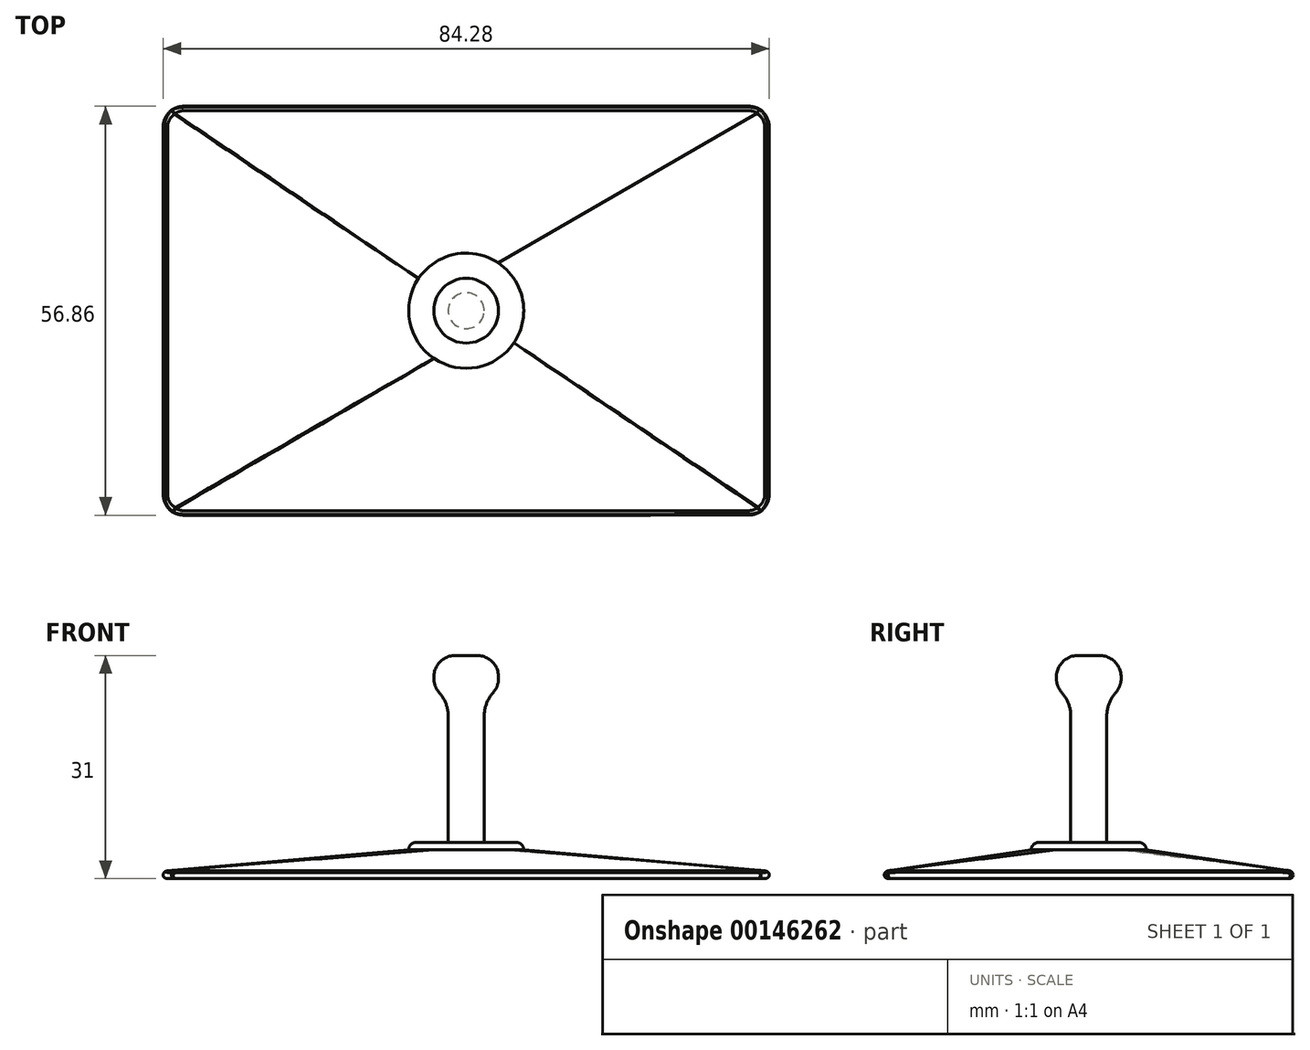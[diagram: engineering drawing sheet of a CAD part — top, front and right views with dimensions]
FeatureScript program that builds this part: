
annotation { "Feature Type Name" : "Feature", "Feature Type Description" : "" }
export const myFeature = defineFeature(function(context is Context, id is Id, definition is map)
    precondition{}
    {
        {
            var Q0;
            Q0=qCreatedBy(makeId("Top.planeOp"),FACE);
            var sketch = newSketch(context, id + "F0", { "sketchPlane" : qUnion([Q0])});
            skLineSegment(sketch, "E0.bottom", {"start": v(42.25, -28.5) * mm, "end": v(-42.25, -28.5) * mm});
            skLineSegment(sketch, "E0.top", {"start": v(42.25, 28.5) * mm, "end": v(-42.25, 28.5) * mm});
            skLineSegment(sketch, "E0.left", {"start": v(42.25, -28.5) * mm, "end": v(42.25, 28.5) * mm});
            skLineSegment(sketch, "E0.right", {"start": v(-42.25, -28.5) * mm, "end": v(-42.25, 28.5) * mm});
            skPoint(sketch, "E0.middle", {"position": v(0, 0) * mm});
            skSolve(sketch);
        }
        {
            var Q0;
            Q0=makeQuery(id+"F0.imprint","IMPRINT",FACE,{"disambiguationData":[TD([[makeQuery(id+"F0.imprint","IMPRINT",EDGE,{"derivedFrom":sQuery(id+"F0.wireOp",EDGE,"E0.bottom")}),-1.0]])]});
            var Q1;
            Q1 = qBodyType(qCreatedBy(id + "F2" ,EDGE), BodyType.WIRE);
            cPlane(context, id + "F1", {"entities" : qUnion([Q0, Q1]), "cplaneType" : CPlaneType.OFFSET, "offset" : 5 * mm, "width" : 150 * mm, "height" : 150 * mm});
        }
        {
            var Q0;
            Q0=qCreatedBy(id+"F1.planeOp",FACE);
            var sketch = newSketch(context, id + "F2", { "sketchPlane" : qUnion([Q0])});
            skCircle(sketch, "E1", {"center": v(0, 0) * mm, "radius": 8 * mm});
            skSolve(sketch);
        }
        {
            var Q0;
            Q0=makeQuery(id+"F2.imprint","IMPRINT",FACE,{"disambiguationData":[TD([[makeQuery(id+"F2.imprint","IMPRINT",EDGE,{"derivedFrom":sQuery(id+"F2.wireOp",EDGE,"E1")}),1.0]])]});
            extrude(context, id + "F3", {"entities" : qUnion([Q0]), "oppositeDirection" : true, "depth" : 1 * mm});
        }
        {
            var Q0;
            Q0=makeQuery(id+"F0.imprint","IMPRINT",FACE,{"disambiguationData":[TD([[makeQuery(id+"F0.imprint","IMPRINT",EDGE,{"derivedFrom":sQuery(id+"F0.wireOp",EDGE,"E0.bottom")}),-1.0]])]});
            extrude(context, id + "F4", {"entities" : qUnion([Q0]), "depth" : 1 * mm});
        }
        {
            var Q1;
            Q1=makeQuery(id+"F4.opExtrude","CAP_FACE",FACE,{"disambiguationData":[OSD([sQuery(id+"F0.wireOp",EDGE,"E0.bottom"),sQuery(id+"F0.wireOp",EDGE,"E0.top"),sQuery(id+"F0.wireOp",EDGE,"E0.left"),sQuery(id+"F0.wireOp",EDGE,"E0.right")])],"isStart":false});
            var Q2;
            Q2=makeQuery(id+"F3.opExtrude","CAP_FACE",FACE,{"disambiguationData":[OSD([sQuery(id+"F2.wireOp",EDGE,"E1")])],"isStart":false});
            loft(context, id + "F5", {"operationType" : NewBodyOperationType.ADD, "sheetProfilesArray" : [{ "sheetProfileEntities" : qUnion([Q1]) }, { "sheetProfileEntities" : qUnion([Q2]) }]});
        }
        {
            var Q0;
            Q0=makeQuery(id+"F3.opExtrude","CAP_FACE",FACE,{"disambiguationData":[OSD([sQuery(id+"F2.wireOp",EDGE,"E1")])],"isStart":true});
            var sketch = newSketch(context, id + "F6", { "sketchPlane" : qUnion([Q0])});
            skCircle(sketch, "E2", {"center": v(0, 0) * mm, "radius": 2.5 * mm});
            skSolve(sketch);
        }
        {
            var Q0;
            Q0 = qSketchRegion(id + "F6", true);
            extrude(context, id + "F7", {"entities" : qUnion([Q0]), "operationType" : NewBodyOperationType.ADD, "depth" : 20 * mm});
        }
        {
            var Q0;
            Q0=makeQuery(id+"F7.opExtrude","CAP_FACE",FACE,{"disambiguationData":[OSD([sQuery(id+"F6.wireOp",EDGE,"E2")])],"isStart":false});
            var sketch = newSketch(context, id + "F8", { "sketchPlane" : qUnion([Q0])});
            skCircle(sketch, "E3", {"center": v(0, 0) * mm, "radius": 4.5 * mm});
            skSolve(sketch);
        }
        {
            var Q0;
            Q0 = qSketchRegion(id + "F8", true);
            extrude(context, id + "F9", {"entities" : qUnion([Q0]), "operationType" : NewBodyOperationType.ADD, "depth" : 6 * mm});
        }
        {
            var Q0;
            Q0=makeQuery(id+"F9.opExtrude","CAP_EDGE",EDGE,{"disambiguationData":[OSD([sQuery(id+"F8.wireOp",EDGE,"E3")])],"isStart":false});
            var Q1;
            Q1=makeQuery(id+"F9.opExtrude","CAP_EDGE",EDGE,{"disambiguationData":[OSD([sQuery(id+"F8.wireOp",EDGE,"E3")])],"isStart":true});
            fillet(context, id + "F10", {"entities" : qUnion([Q0, Q1]), "radius" : 3 * mm, "tangentPropagation" : true, "allowEdgeOverflow" : false});
        }
        {
            var Q0;
            Q0=makeQuery(id+"F10.opFillet","BLEND_EDGE",EDGE,{"blendedFrom":[makeQuery(id+"F9.opExtrude","CAP_EDGE",EDGE,{"disambiguationData":[OSD([sQuery(id+"F8.wireOp",EDGE,"E3")])],"isStart":true}),makeQuery(id+"F7.opExtrude","SWEPT_FACE",FACE,{"disambiguationData":[OSD([sQuery(id+"F6.wireOp",EDGE,"E2")])]})],"blendedInto":[makeQuery(id+"F7.opExtrude","SWEPT_FACE",FACE,{"disambiguationData":[OSD([sQuery(id+"F6.wireOp",EDGE,"E2")])]})]});
            var Q1;
            Q1=makeQuery(id+"F7.opExtrude","CAP_EDGE",EDGE,{"disambiguationData":[OSD([sQuery(id+"F6.wireOp",EDGE,"E2")])],"isStart":true});
            fillet(context, id + "F11", {"entities" : qUnion([Q0, Q1]), "radius" : 5 * mm, "tangentPropagation" : true, "allowEdgeOverflow" : false});
        }
        {
            var Q0;
            Q0=makeQuery(id+"F3.opExtrude","CAP_EDGE",EDGE,{"disambiguationData":[OSD([sQuery(id+"F2.wireOp",EDGE,"E1")])],"isStart":true});
            fillet(context, id + "F12", {"entities" : qUnion([Q0]), "radius" : 1 * mm, "tangentPropagation" : true, "allowEdgeOverflow" : false});
        }
        {
            var Q0;
            Q0=makeQuery(id+"F5.opLoft","SWEPT_EDGE",EDGE,{"disambiguationData":[OSD([sQuery(id+"F0.wireOp",EDGE,"E0.bottom"),sQuery(id+"F0.wireOp",EDGE,"E0.left")])]});
            var Q1;
            Q1=makeQuery(id+"F5.opLoft","SWEPT_EDGE",EDGE,{"disambiguationData":[OSD([sQuery(id+"F0.wireOp",EDGE,"E0.bottom"),sQuery(id+"F0.wireOp",EDGE,"E0.top"),sQuery(id+"F0.wireOp",EDGE,"E0.right"),sQuery(id+"F2.wireOp",EDGE,"E1")])]});
            var Q2;
            Q2=makeQuery(id+"F5.opLoft","SWEPT_EDGE",EDGE,{"disambiguationData":[OSD([sQuery(id+"F0.wireOp",EDGE,"E0.bottom"),sQuery(id+"F0.wireOp",EDGE,"E0.top"),sQuery(id+"F0.wireOp",EDGE,"E0.left"),sQuery(id+"F2.wireOp",EDGE,"E1")])]});
            var Q3;
            Q3=makeQuery(id+"F5.opLoft","SWEPT_EDGE",EDGE,{"disambiguationData":[OSD([sQuery(id+"F0.wireOp",EDGE,"E0.top"),sQuery(id+"F0.wireOp",EDGE,"E0.left"),sQuery(id+"F0.wireOp",EDGE,"E0.right"),sQuery(id+"F2.wireOp",EDGE,"E1")])]});
            fillet(context, id + "F13", {"entities" : qUnion([Q0, Q1, Q2, Q3]), "radius" : 1 * mm, "tangentPropagation" : true, "allowEdgeOverflow" : false});
        }
        {
            var Q0;
            Q0=makeQuery(id+"F4.opExtrude","SWEPT_EDGE",EDGE,{"disambiguationData":[OSD([sQuery(id+"F0.wireOp",EDGE,"E0.bottom"),sQuery(id+"F0.wireOp",EDGE,"E0.right")])]});
            var Q1;
            Q1=makeQuery(id+"F4.opExtrude","SWEPT_EDGE",EDGE,{"disambiguationData":[OSD([sQuery(id+"F0.wireOp",EDGE,"E0.top"),sQuery(id+"F0.wireOp",EDGE,"E0.right")])]});
            var Q2;
            Q2=makeQuery(id+"F4.opExtrude","SWEPT_EDGE",EDGE,{"disambiguationData":[OSD([sQuery(id+"F0.wireOp",EDGE,"E0.bottom"),sQuery(id+"F0.wireOp",EDGE,"E0.left")])]});
            var Q3;
            Q3=makeQuery(id+"F4.opExtrude","SWEPT_EDGE",EDGE,{"disambiguationData":[OSD([sQuery(id+"F0.wireOp",EDGE,"E0.top"),sQuery(id+"F0.wireOp",EDGE,"E0.left")])]});
            fillet(context, id + "F14", {"entities" : qUnion([Q0, Q1, Q2, Q3]), "radius" : 3 * mm, "tangentPropagation" : true, "allowEdgeOverflow" : false});
        }
        {
            var Q0;
            {var subQ0=sQuery(id+"F0.wireOp",EDGE,"E0.right");Q0=makeQuery(id+"F5.boolean.opBoolean","MERGE",EDGE,{"derivedFrom":[makeQuery(id+"F4.opExtrude","CAP_EDGE",EDGE,{"disambiguationData":[OSD([subQ0])],"isStart":false}),makeQuery(id+"F5.opLoft","MID_CAP_EDGE",EDGE,{"disambiguationData":[OSD([sQuery(id+"F0.wireOp",EDGE,"E0.bottom"),sQuery(id+"F0.wireOp",EDGE,"E0.top"),subQ0])],"capPos":0.0})]});}
            var Q1;
            {var subQ0=sQuery(id+"F0.wireOp",EDGE,"E0.right");var subQ1=sQuery(id+"F0.wireOp",EDGE,"E0.top");var subQ2=sQuery(id+"F0.wireOp",EDGE,"E0.left");var subQ3=sQuery(id+"F0.wireOp",EDGE,"E0.bottom");var subQ4=sQuery(id+"F2.wireOp",EDGE,"E1");Q1=makeQuery(id+"F14.opFillet","BLEND_EDGE",EDGE,{"blendedFrom":[makeQuery(id+"F4.opExtrude","SWEPT_EDGE",EDGE,{"disambiguationData":[OSD([subQ3,subQ0])]}),makeQuery(id+"F5.opLoft","SWEPT_FACE",FACE,{"disambiguationData":[OSD([subQ3,subQ1,subQ2,subQ0,subQ4]),TDD([makeQuery(id+"F3.opExtrude","CAP_EDGE",EDGE,{"disambiguationData":[OSD([subQ4])],"isStart":false}),makeQuery(id+"F4.opExtrude","CAP_VERTEX",VERTEX,{"disambiguationData":[OSD([subQ3,subQ0])],"isStart":false}),makeQuery(id+"F4.opExtrude","CAP_VERTEX",VERTEX,{"disambiguationData":[OSD([subQ1,subQ2])],"isStart":false}),makeQuery(id+"F4.opExtrude","CAP_VERTEX",VERTEX,{"disambiguationData":[OSD([subQ1,subQ0])],"isStart":false}),makeQuery(id+"F4.opExtrude","CAP_EDGE",EDGE,{"disambiguationData":[OSD([subQ0])],"isStart":false})])]})],"blendedInto":[makeQuery(id+"F5.opLoft","SWEPT_FACE",FACE,{"disambiguationData":[OSD([subQ3,subQ1,subQ2,subQ0,subQ4]),TDD([makeQuery(id+"F3.opExtrude","CAP_EDGE",EDGE,{"disambiguationData":[OSD([subQ4])],"isStart":false}),makeQuery(id+"F4.opExtrude","CAP_VERTEX",VERTEX,{"disambiguationData":[OSD([subQ3,subQ0])],"isStart":false}),makeQuery(id+"F4.opExtrude","CAP_VERTEX",VERTEX,{"disambiguationData":[OSD([subQ1,subQ2])],"isStart":false}),makeQuery(id+"F4.opExtrude","CAP_VERTEX",VERTEX,{"disambiguationData":[OSD([subQ1,subQ0])],"isStart":false}),makeQuery(id+"F4.opExtrude","CAP_EDGE",EDGE,{"disambiguationData":[OSD([subQ0])],"isStart":false})])]})]});}
            var Q2;
            {var subQ0=sQuery(id+"F0.wireOp",EDGE,"E0.bottom");var subQ1=sQuery(id+"F0.wireOp",EDGE,"E0.right");var subQ2=sQuery(id+"F0.wireOp",EDGE,"E0.top");var subQ3=sQuery(id+"F0.wireOp",EDGE,"E0.left");var subQ4=sQuery(id+"F2.wireOp",EDGE,"E1");Q2=makeQuery(id+"F14.opFillet","BLEND_EDGE",EDGE,{"blendedFrom":[makeQuery(id+"F4.opExtrude","SWEPT_EDGE",EDGE,{"disambiguationData":[OSD([subQ0,subQ1])]}),makeQuery(id+"F5.opLoft","SWEPT_FACE",FACE,{"disambiguationData":[OSD([subQ0,subQ2,subQ3,subQ1,subQ4]),TDD([makeQuery(id+"F3.opExtrude","CAP_EDGE",EDGE,{"disambiguationData":[OSD([subQ4])],"isStart":false}),makeQuery(id+"F4.opExtrude","CAP_VERTEX",VERTEX,{"disambiguationData":[OSD([subQ0,subQ3])],"isStart":false}),makeQuery(id+"F4.opExtrude","CAP_VERTEX",VERTEX,{"disambiguationData":[OSD([subQ0,subQ1])],"isStart":false}),makeQuery(id+"F4.opExtrude","CAP_VERTEX",VERTEX,{"disambiguationData":[OSD([subQ2,subQ1])],"isStart":false}),makeQuery(id+"F4.opExtrude","CAP_EDGE",EDGE,{"disambiguationData":[OSD([subQ0])],"isStart":false})])]})],"blendedInto":[makeQuery(id+"F5.opLoft","SWEPT_FACE",FACE,{"disambiguationData":[OSD([subQ0,subQ2,subQ3,subQ1,subQ4]),TDD([makeQuery(id+"F3.opExtrude","CAP_EDGE",EDGE,{"disambiguationData":[OSD([subQ4])],"isStart":false}),makeQuery(id+"F4.opExtrude","CAP_VERTEX",VERTEX,{"disambiguationData":[OSD([subQ0,subQ3])],"isStart":false}),makeQuery(id+"F4.opExtrude","CAP_VERTEX",VERTEX,{"disambiguationData":[OSD([subQ0,subQ1])],"isStart":false}),makeQuery(id+"F4.opExtrude","CAP_VERTEX",VERTEX,{"disambiguationData":[OSD([subQ2,subQ1])],"isStart":false}),makeQuery(id+"F4.opExtrude","CAP_EDGE",EDGE,{"disambiguationData":[OSD([subQ0])],"isStart":false})])]})]});}
            var Q3;
            {var subQ0=sQuery(id+"F0.wireOp",EDGE,"E0.bottom");Q3=makeQuery(id+"F5.boolean.opBoolean","MERGE",EDGE,{"derivedFrom":[makeQuery(id+"F4.opExtrude","CAP_EDGE",EDGE,{"disambiguationData":[OSD([subQ0])],"isStart":false}),makeQuery(id+"F5.opLoft","MID_CAP_EDGE",EDGE,{"disambiguationData":[OSD([subQ0,sQuery(id+"F0.wireOp",EDGE,"E0.left"),sQuery(id+"F0.wireOp",EDGE,"E0.right")])],"capPos":0.0})]});}
            var Q4;
            {var subQ0=sQuery(id+"F0.wireOp",EDGE,"E0.bottom");var subQ1=sQuery(id+"F0.wireOp",EDGE,"E0.right");var subQ2=sQuery(id+"F0.wireOp",EDGE,"E0.top");var subQ3=sQuery(id+"F0.wireOp",EDGE,"E0.left");var subQ4=sQuery(id+"F2.wireOp",EDGE,"E1");Q4=makeQuery(id+"F14.opFillet","BLEND_EDGE",EDGE,{"blendedFrom":[makeQuery(id+"F4.opExtrude","SWEPT_EDGE",EDGE,{"disambiguationData":[OSD([subQ0,subQ3])]}),makeQuery(id+"F5.opLoft","SWEPT_FACE",FACE,{"disambiguationData":[OSD([subQ0,subQ2,subQ3,subQ1,subQ4]),TDD([makeQuery(id+"F3.opExtrude","CAP_EDGE",EDGE,{"disambiguationData":[OSD([subQ4])],"isStart":false}),makeQuery(id+"F4.opExtrude","CAP_VERTEX",VERTEX,{"disambiguationData":[OSD([subQ0,subQ3])],"isStart":false}),makeQuery(id+"F4.opExtrude","CAP_VERTEX",VERTEX,{"disambiguationData":[OSD([subQ0,subQ1])],"isStart":false}),makeQuery(id+"F4.opExtrude","CAP_VERTEX",VERTEX,{"disambiguationData":[OSD([subQ2,subQ1])],"isStart":false}),makeQuery(id+"F4.opExtrude","CAP_EDGE",EDGE,{"disambiguationData":[OSD([subQ0])],"isStart":false})])]})],"blendedInto":[makeQuery(id+"F5.opLoft","SWEPT_FACE",FACE,{"disambiguationData":[OSD([subQ0,subQ2,subQ3,subQ1,subQ4]),TDD([makeQuery(id+"F3.opExtrude","CAP_EDGE",EDGE,{"disambiguationData":[OSD([subQ4])],"isStart":false}),makeQuery(id+"F4.opExtrude","CAP_VERTEX",VERTEX,{"disambiguationData":[OSD([subQ0,subQ3])],"isStart":false}),makeQuery(id+"F4.opExtrude","CAP_VERTEX",VERTEX,{"disambiguationData":[OSD([subQ0,subQ1])],"isStart":false}),makeQuery(id+"F4.opExtrude","CAP_VERTEX",VERTEX,{"disambiguationData":[OSD([subQ2,subQ1])],"isStart":false}),makeQuery(id+"F4.opExtrude","CAP_EDGE",EDGE,{"disambiguationData":[OSD([subQ0])],"isStart":false})])]})]});}
            var Q5;
            {var subQ0=sQuery(id+"F0.wireOp",EDGE,"E0.left");var subQ1=sQuery(id+"F0.wireOp",EDGE,"E0.bottom");Q5=makeQuery(id+"F14.opFillet","BLEND_EDGE",EDGE,{"blendedFrom":[makeQuery(id+"F4.opExtrude","SWEPT_EDGE",EDGE,{"disambiguationData":[OSD([subQ1,subQ0])]}),makeQuery(id+"F5.opLoft","SWEPT_FACE",FACE,{"disambiguationData":[OSD([subQ1,sQuery(id+"F0.wireOp",EDGE,"E0.top"),subQ0,sQuery(id+"F2.wireOp",EDGE,"E1")])]})],"blendedInto":[makeQuery(id+"F5.opLoft","SWEPT_FACE",FACE,{"disambiguationData":[OSD([subQ1,sQuery(id+"F0.wireOp",EDGE,"E0.top"),subQ0,sQuery(id+"F2.wireOp",EDGE,"E1")])]})]});}
            var Q6;
            {var subQ0=sQuery(id+"F0.wireOp",EDGE,"E0.left");Q6=makeQuery(id+"F5.boolean.opBoolean","MERGE",EDGE,{"derivedFrom":[makeQuery(id+"F4.opExtrude","CAP_EDGE",EDGE,{"disambiguationData":[OSD([subQ0])],"isStart":false}),makeQuery(id+"F5.opLoft","MID_CAP_EDGE",EDGE,{"disambiguationData":[OSD([sQuery(id+"F0.wireOp",EDGE,"E0.bottom"),sQuery(id+"F0.wireOp",EDGE,"E0.top"),subQ0])],"capPos":0.0})]});}
            var Q7;
            {var subQ0=sQuery(id+"F0.wireOp",EDGE,"E0.left");var subQ1=sQuery(id+"F0.wireOp",EDGE,"E0.top");Q7=makeQuery(id+"F14.opFillet","BLEND_EDGE",EDGE,{"blendedFrom":[makeQuery(id+"F4.opExtrude","SWEPT_EDGE",EDGE,{"disambiguationData":[OSD([subQ1,subQ0])]}),makeQuery(id+"F5.opLoft","SWEPT_FACE",FACE,{"disambiguationData":[OSD([sQuery(id+"F0.wireOp",EDGE,"E0.bottom"),subQ1,subQ0,sQuery(id+"F2.wireOp",EDGE,"E1")])]})],"blendedInto":[makeQuery(id+"F5.opLoft","SWEPT_FACE",FACE,{"disambiguationData":[OSD([sQuery(id+"F0.wireOp",EDGE,"E0.bottom"),subQ1,subQ0,sQuery(id+"F2.wireOp",EDGE,"E1")])]})]});}
            var Q8;
            {var subQ0=sQuery(id+"F0.wireOp",EDGE,"E0.top");Q8=makeQuery(id+"F5.boolean.opBoolean","MERGE",EDGE,{"derivedFrom":[makeQuery(id+"F4.opExtrude","CAP_EDGE",EDGE,{"disambiguationData":[OSD([subQ0])],"isStart":false}),makeQuery(id+"F5.opLoft","MID_CAP_EDGE",EDGE,{"disambiguationData":[OSD([subQ0,sQuery(id+"F0.wireOp",EDGE,"E0.left"),sQuery(id+"F0.wireOp",EDGE,"E0.right")])],"capPos":0.0})]});}
            var Q9;
            {var subQ0=sQuery(id+"F0.wireOp",EDGE,"E0.top");var subQ1=sQuery(id+"F0.wireOp",EDGE,"E0.right");var subQ2=sQuery(id+"F0.wireOp",EDGE,"E0.left");var subQ3=sQuery(id+"F0.wireOp",EDGE,"E0.bottom");var subQ4=sQuery(id+"F2.wireOp",EDGE,"E1");Q9=makeQuery(id+"F14.opFillet","BLEND_EDGE",EDGE,{"blendedFrom":[makeQuery(id+"F4.opExtrude","SWEPT_EDGE",EDGE,{"disambiguationData":[OSD([subQ0,subQ2])]}),makeQuery(id+"F5.opLoft","SWEPT_FACE",FACE,{"disambiguationData":[OSD([subQ3,subQ0,subQ2,subQ1,subQ4]),TDD([makeQuery(id+"F3.opExtrude","CAP_EDGE",EDGE,{"disambiguationData":[OSD([subQ4])],"isStart":false}),makeQuery(id+"F4.opExtrude","CAP_VERTEX",VERTEX,{"disambiguationData":[OSD([subQ3,subQ2])],"isStart":false}),makeQuery(id+"F4.opExtrude","CAP_VERTEX",VERTEX,{"disambiguationData":[OSD([subQ0,subQ2])],"isStart":false}),makeQuery(id+"F4.opExtrude","CAP_VERTEX",VERTEX,{"disambiguationData":[OSD([subQ0,subQ1])],"isStart":false}),makeQuery(id+"F4.opExtrude","CAP_EDGE",EDGE,{"disambiguationData":[OSD([subQ0])],"isStart":false})])]})],"blendedInto":[makeQuery(id+"F5.opLoft","SWEPT_FACE",FACE,{"disambiguationData":[OSD([subQ3,subQ0,subQ2,subQ1,subQ4]),TDD([makeQuery(id+"F3.opExtrude","CAP_EDGE",EDGE,{"disambiguationData":[OSD([subQ4])],"isStart":false}),makeQuery(id+"F4.opExtrude","CAP_VERTEX",VERTEX,{"disambiguationData":[OSD([subQ3,subQ2])],"isStart":false}),makeQuery(id+"F4.opExtrude","CAP_VERTEX",VERTEX,{"disambiguationData":[OSD([subQ0,subQ2])],"isStart":false}),makeQuery(id+"F4.opExtrude","CAP_VERTEX",VERTEX,{"disambiguationData":[OSD([subQ0,subQ1])],"isStart":false}),makeQuery(id+"F4.opExtrude","CAP_EDGE",EDGE,{"disambiguationData":[OSD([subQ0])],"isStart":false})])]})]});}
            var Q10;
            {var subQ0=sQuery(id+"F0.wireOp",EDGE,"E0.top");var subQ1=sQuery(id+"F0.wireOp",EDGE,"E0.right");var subQ2=sQuery(id+"F0.wireOp",EDGE,"E0.left");var subQ3=sQuery(id+"F0.wireOp",EDGE,"E0.bottom");var subQ4=sQuery(id+"F2.wireOp",EDGE,"E1");Q10=makeQuery(id+"F14.opFillet","BLEND_EDGE",EDGE,{"blendedFrom":[makeQuery(id+"F4.opExtrude","SWEPT_EDGE",EDGE,{"disambiguationData":[OSD([subQ0,subQ1])]}),makeQuery(id+"F5.opLoft","SWEPT_FACE",FACE,{"disambiguationData":[OSD([subQ3,subQ0,subQ2,subQ1,subQ4]),TDD([makeQuery(id+"F3.opExtrude","CAP_EDGE",EDGE,{"disambiguationData":[OSD([subQ4])],"isStart":false}),makeQuery(id+"F4.opExtrude","CAP_VERTEX",VERTEX,{"disambiguationData":[OSD([subQ3,subQ2])],"isStart":false}),makeQuery(id+"F4.opExtrude","CAP_VERTEX",VERTEX,{"disambiguationData":[OSD([subQ0,subQ2])],"isStart":false}),makeQuery(id+"F4.opExtrude","CAP_VERTEX",VERTEX,{"disambiguationData":[OSD([subQ0,subQ1])],"isStart":false}),makeQuery(id+"F4.opExtrude","CAP_EDGE",EDGE,{"disambiguationData":[OSD([subQ0])],"isStart":false})])]})],"blendedInto":[makeQuery(id+"F5.opLoft","SWEPT_FACE",FACE,{"disambiguationData":[OSD([subQ3,subQ0,subQ2,subQ1,subQ4]),TDD([makeQuery(id+"F3.opExtrude","CAP_EDGE",EDGE,{"disambiguationData":[OSD([subQ4])],"isStart":false}),makeQuery(id+"F4.opExtrude","CAP_VERTEX",VERTEX,{"disambiguationData":[OSD([subQ3,subQ2])],"isStart":false}),makeQuery(id+"F4.opExtrude","CAP_VERTEX",VERTEX,{"disambiguationData":[OSD([subQ0,subQ2])],"isStart":false}),makeQuery(id+"F4.opExtrude","CAP_VERTEX",VERTEX,{"disambiguationData":[OSD([subQ0,subQ1])],"isStart":false}),makeQuery(id+"F4.opExtrude","CAP_EDGE",EDGE,{"disambiguationData":[OSD([subQ0])],"isStart":false})])]})]});}
            var Q11;
            {var subQ0=sQuery(id+"F0.wireOp",EDGE,"E0.right");var subQ1=sQuery(id+"F0.wireOp",EDGE,"E0.top");var subQ2=sQuery(id+"F0.wireOp",EDGE,"E0.left");var subQ3=sQuery(id+"F0.wireOp",EDGE,"E0.bottom");var subQ4=sQuery(id+"F2.wireOp",EDGE,"E1");Q11=makeQuery(id+"F14.opFillet","BLEND_EDGE",EDGE,{"blendedFrom":[makeQuery(id+"F4.opExtrude","SWEPT_EDGE",EDGE,{"disambiguationData":[OSD([subQ1,subQ0])]}),makeQuery(id+"F5.opLoft","SWEPT_FACE",FACE,{"disambiguationData":[OSD([subQ3,subQ1,subQ2,subQ0,subQ4]),TDD([makeQuery(id+"F3.opExtrude","CAP_EDGE",EDGE,{"disambiguationData":[OSD([subQ4])],"isStart":false}),makeQuery(id+"F4.opExtrude","CAP_VERTEX",VERTEX,{"disambiguationData":[OSD([subQ3,subQ0])],"isStart":false}),makeQuery(id+"F4.opExtrude","CAP_VERTEX",VERTEX,{"disambiguationData":[OSD([subQ1,subQ2])],"isStart":false}),makeQuery(id+"F4.opExtrude","CAP_VERTEX",VERTEX,{"disambiguationData":[OSD([subQ1,subQ0])],"isStart":false}),makeQuery(id+"F4.opExtrude","CAP_EDGE",EDGE,{"disambiguationData":[OSD([subQ0])],"isStart":false})])]})],"blendedInto":[makeQuery(id+"F5.opLoft","SWEPT_FACE",FACE,{"disambiguationData":[OSD([subQ3,subQ1,subQ2,subQ0,subQ4]),TDD([makeQuery(id+"F3.opExtrude","CAP_EDGE",EDGE,{"disambiguationData":[OSD([subQ4])],"isStart":false}),makeQuery(id+"F4.opExtrude","CAP_VERTEX",VERTEX,{"disambiguationData":[OSD([subQ3,subQ0])],"isStart":false}),makeQuery(id+"F4.opExtrude","CAP_VERTEX",VERTEX,{"disambiguationData":[OSD([subQ1,subQ2])],"isStart":false}),makeQuery(id+"F4.opExtrude","CAP_VERTEX",VERTEX,{"disambiguationData":[OSD([subQ1,subQ0])],"isStart":false}),makeQuery(id+"F4.opExtrude","CAP_EDGE",EDGE,{"disambiguationData":[OSD([subQ0])],"isStart":false})])]})]});}
            fillet(context, id + "F15", {"entities" : qUnion([Q0, Q1, Q2, Q3, Q4, Q5, Q6, Q7, Q8, Q9, Q10, Q11]), "radius" : .8 * mm, "tangentPropagation" : true, "allowEdgeOverflow" : false});
        }
        {
            var Q0;
            {var subQ0=sQuery(id+"F0.wireOp",EDGE,"E0.right");var subQ1=sQuery(id+"F0.wireOp",EDGE,"E0.bottom");Q0=makeQuery(id+"F14.opFillet","BLEND_EDGE",EDGE,{"blendedFrom":[makeQuery(id+"F4.opExtrude","SWEPT_EDGE",EDGE,{"disambiguationData":[OSD([subQ1,subQ0])]}),makeQuery(id+"F4.opExtrude","CAP_FACE",FACE,{"disambiguationData":[OSD([subQ1,sQuery(id+"F0.wireOp",EDGE,"E0.top"),sQuery(id+"F0.wireOp",EDGE,"E0.left"),subQ0])],"isStart":true})],"blendedInto":[makeQuery(id+"F4.opExtrude","CAP_FACE",FACE,{"disambiguationData":[OSD([subQ1,sQuery(id+"F0.wireOp",EDGE,"E0.top"),sQuery(id+"F0.wireOp",EDGE,"E0.left"),subQ0])],"isStart":true})]});}
            var Q1;
            {var subQ0=sQuery(id+"F0.wireOp",EDGE,"E0.left");var subQ1=sQuery(id+"F0.wireOp",EDGE,"E0.top");Q1=makeQuery(id+"F14.opFillet","BLEND_EDGE",EDGE,{"blendedFrom":[makeQuery(id+"F4.opExtrude","SWEPT_EDGE",EDGE,{"disambiguationData":[OSD([subQ1,subQ0])]}),makeQuery(id+"F4.opExtrude","CAP_FACE",FACE,{"disambiguationData":[OSD([sQuery(id+"F0.wireOp",EDGE,"E0.bottom"),subQ1,subQ0,sQuery(id+"F0.wireOp",EDGE,"E0.right")])],"isStart":true})],"blendedInto":[makeQuery(id+"F4.opExtrude","CAP_FACE",FACE,{"disambiguationData":[OSD([sQuery(id+"F0.wireOp",EDGE,"E0.bottom"),subQ1,subQ0,sQuery(id+"F0.wireOp",EDGE,"E0.right")])],"isStart":true})]});}
            var Q2;
            {var subQ0=sQuery(id+"F0.wireOp",EDGE,"E0.left");var subQ1=sQuery(id+"F0.wireOp",EDGE,"E0.bottom");Q2=makeQuery(id+"F14.opFillet","BLEND_EDGE",EDGE,{"blendedFrom":[makeQuery(id+"F4.opExtrude","SWEPT_EDGE",EDGE,{"disambiguationData":[OSD([subQ1,subQ0])]}),makeQuery(id+"F4.opExtrude","CAP_FACE",FACE,{"disambiguationData":[OSD([subQ1,sQuery(id+"F0.wireOp",EDGE,"E0.top"),subQ0,sQuery(id+"F0.wireOp",EDGE,"E0.right")])],"isStart":true})],"blendedInto":[makeQuery(id+"F4.opExtrude","CAP_FACE",FACE,{"disambiguationData":[OSD([subQ1,sQuery(id+"F0.wireOp",EDGE,"E0.top"),subQ0,sQuery(id+"F0.wireOp",EDGE,"E0.right")])],"isStart":true})]});}
            var Q3;
            {var subQ0=sQuery(id+"F0.wireOp",EDGE,"E0.right");var subQ1=sQuery(id+"F0.wireOp",EDGE,"E0.top");Q3=makeQuery(id+"F14.opFillet","BLEND_EDGE",EDGE,{"blendedFrom":[makeQuery(id+"F4.opExtrude","SWEPT_EDGE",EDGE,{"disambiguationData":[OSD([subQ1,subQ0])]}),makeQuery(id+"F4.opExtrude","CAP_FACE",FACE,{"disambiguationData":[OSD([sQuery(id+"F0.wireOp",EDGE,"E0.bottom"),subQ1,sQuery(id+"F0.wireOp",EDGE,"E0.left"),subQ0])],"isStart":true})],"blendedInto":[makeQuery(id+"F4.opExtrude","CAP_FACE",FACE,{"disambiguationData":[OSD([sQuery(id+"F0.wireOp",EDGE,"E0.bottom"),subQ1,sQuery(id+"F0.wireOp",EDGE,"E0.left"),subQ0])],"isStart":true})]});}
            var Q4;
            Q4=makeQuery(id+"F4.opExtrude","CAP_EDGE",EDGE,{"disambiguationData":[OSD([sQuery(id+"F0.wireOp",EDGE,"E0.right")])],"isStart":true});
            var Q5;
            Q5=makeQuery(id+"F4.opExtrude","CAP_EDGE",EDGE,{"disambiguationData":[OSD([sQuery(id+"F0.wireOp",EDGE,"E0.bottom")])],"isStart":true});
            var Q6;
            Q6=makeQuery(id+"F4.opExtrude","CAP_EDGE",EDGE,{"disambiguationData":[OSD([sQuery(id+"F0.wireOp",EDGE,"E0.top")])],"isStart":true});
            var Q7;
            Q7=makeQuery(id+"F4.opExtrude","CAP_EDGE",EDGE,{"disambiguationData":[OSD([sQuery(id+"F0.wireOp",EDGE,"E0.left")])],"isStart":true});
            fillet(context, id + "F16", {"entities" : qUnion([Q0, Q1, Q2, Q3, Q4, Q5, Q6, Q7]), "radius" : .5 * mm, "tangentPropagation" : true, "allowEdgeOverflow" : false});
        }
    });
